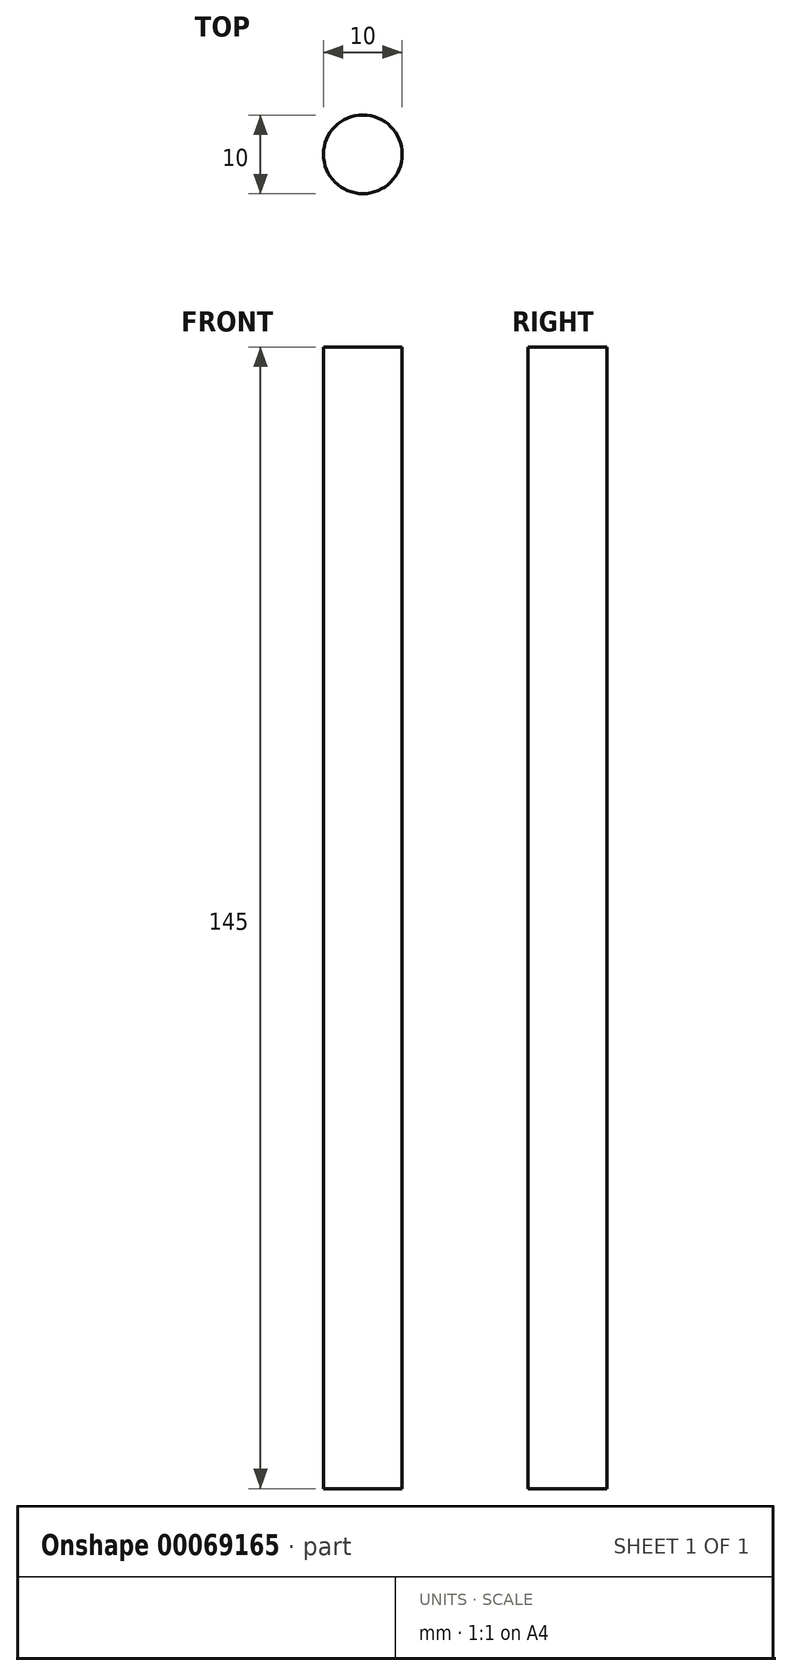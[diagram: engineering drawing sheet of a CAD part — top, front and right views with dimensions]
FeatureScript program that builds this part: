
annotation { "Feature Type Name" : "Feature", "Feature Type Description" : "" }
export const myFeature = defineFeature(function(context is Context, id is Id, definition is map)
    precondition{}
    {
        {
            var Q0;
            Q0=qCreatedBy(makeId("Top.planeOp"),FACE);
            var sketch = newSketch(context, id + "F0", { "sketchPlane" : qUnion([Q0])});
            skCircle(sketch, "E0", {"center": v(0, 0) * mm, "radius": 5 * mm});
            skSolve(sketch);
        }
        {
            var Q0;
            Q0 = qSketchRegion(id + "F0", true);
            extrude(context, id + "F1", {"entities" : qUnion([Q0]), "flatOperationType" : FlatOperationType.REMOVE, "offsetDistance" : 25 * mm, "depth" : 60 * mm, "domain" : OperationDomain.MODEL});
        }
        {
            var Q0;
            Q0=makeQuery(id+"F1.opExtrude","CAP_FACE",FACE,{"disambiguationData":[OSD([sQuery(id+"F0.wireOp",EDGE,"E0")])],"isStart":false});
            var sketch = newSketch(context, id + "F2", { "sketchPlane" : qUnion([Q0])});
            skCircle(sketch, "E1", {"center": v(0, 0) * mm, "radius": 5 * mm});
            skSolve(sketch);
        }
        {
            var Q0;
            Q0 = qSketchRegion(id + "F2", true);
            extrude(context, id + "F3", {"entities" : qUnion([Q0]), "operationType" : NewBodyOperationType.ADD, "depth" : 85 * mm});
        }
    });
